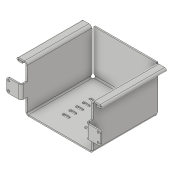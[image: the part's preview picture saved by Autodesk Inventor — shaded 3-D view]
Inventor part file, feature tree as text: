
AUTODESK INVENTOR PART (.ipt)
format: ipt  version: 2017 (Build 210142000, 142)  size: 476,672 bytes
history: native  units: in
note: dims shown in document units (in); Inventor stores cm internally (conversion verified against a paired STEP export)
features: sheet_metal_op x13, sketch x6, other x6, hole x2, pattern_linear x1, plane x1, chamfer x1, mirror x1
ambient origin geometry x8: Origin, YZ Plane, XZ Plane, XY Plane, X Axis, Y Axis, Z Axis, Center Point
bodies: Solid1 (feature_tree)
feature tree (31):
  sheet_metal_op  "Face1"
  sheet_metal_op  "Flange1"
  sheet_metal_op  "Contour Flange1"
  pattern_linear  "Rectangular Pattern1"  Spacing1=0.12in  [1 undecoded]
  plane  "Work Plane1"
  sheet_metal_op  "Face2"
  sheet_metal_op  "Bend4"
  chamfer  "Corner Round1"
  hole  "Hole1"  [1 undecoded]
  hole  "Hole2"  [1 undecoded]
  sheet_metal_op  "Hem1"
  mirror  "Mirror1"
  sketch  "Sketch1"  dims[d0=6.0in]
  other  "Plate1"
  sketch  "Sketch2"  dims[d1=6.0in]
  other  "Plate2"
  sheet_metal_op  "Bend1"
  sheet_metal_op  "Corner1"
  sketch  "Sketch3"  dims[d2=0.12in]
  other  "Plate3"
  sheet_metal_op  "Bend2"
  sheet_metal_op  "Corner2"
  sketch  "Sketch4"  dims[d3=0.12in]
  sketch  "Sketch5"  dims[d4=0.06in]
  other  "Plate4"
  sheet_metal_op  "Bend3"
  sheet_metal_op  "Corner3"
  other  "iFeature1:1"
  sheet_metal_op  "Corner4"
  sketch  "Sketch6"  dims[d5=0.24in d6=0.12in d7=4.0in d8=90.0deg d9=0.12in d10=0.48in d11=0.12in d12=0.12in d13=0.8in d15=3.88in d16=0.12in d17=0.06in d18=0.24in d19=0.12in d20=0.12in d21=0.12in d22=0.48in d23=0.12in d24=0.12in d25=0.48in d26=0.12in d27=0.12in d28=0.0in d29=0.3937in d30=4.0in d31=4.0in d32=0.45in d34=0.1in d36=90.0deg d37=1.9685in d39=0.6in d40=0.7874in d42=2.0in d43=6.3in d44=0.8in d45=1.2in d46=0.4in d47=1.38in d48=0.12in d49=0.12in d50=0.06in d51=0.24in d52=0.12in d53=0.12in d54=0.06in d55=0.24in d56=0.12in d57=0.12in d58=0.2in d59=1.0in d60=1.0in d61=0.12in d62=0.75in d63=0.2in d64=0.25in d65=90.0deg d66=0.12in d67=0.8108in d68=1.0in d69=1.0in d70=0.12in d71=0.75in d72=0.2in d73=0.25in d74=90.0deg d75=0.12in d76=0.8108in d77=0.12in d78=0.06in d79=0.24in d80=0.12in d81=0.48in d82=0.06in d83=0.03in d84=0.48in d85=0.12in d86=0.12in d87=0.0in d88=0.3937in]
  other  "Definition1"
note: 3 required parameter values undecoded (feature->parameter linkage not recoverable at this tier; creation-order binding heuristic only, values carry confidence <= 0.55)
